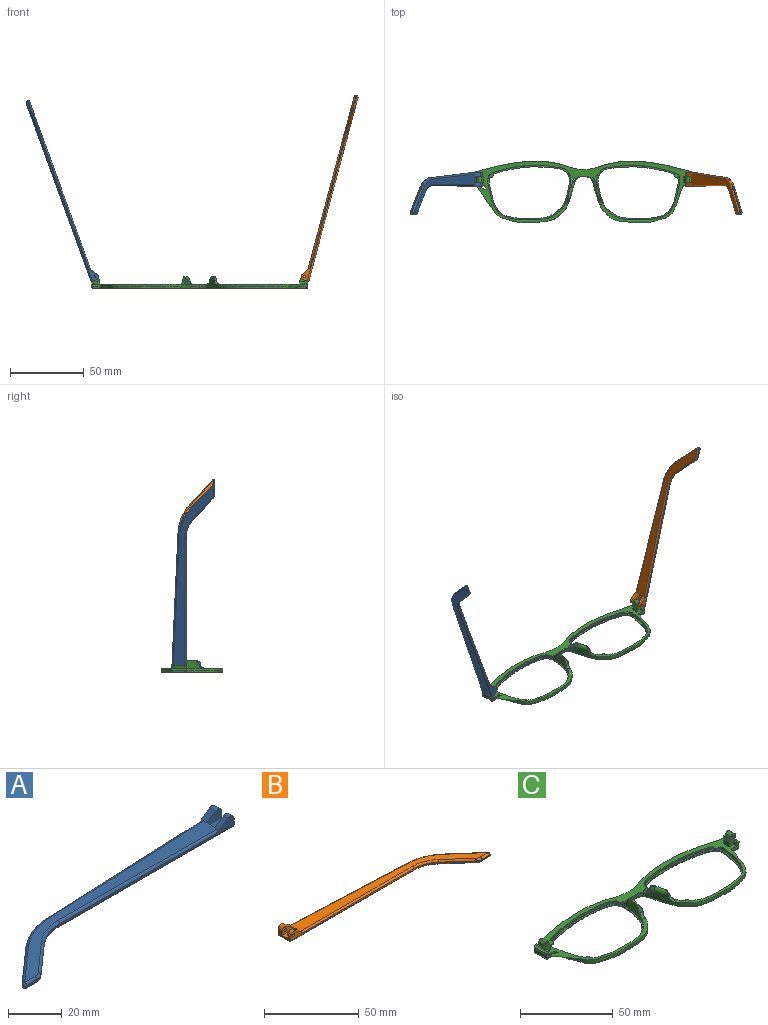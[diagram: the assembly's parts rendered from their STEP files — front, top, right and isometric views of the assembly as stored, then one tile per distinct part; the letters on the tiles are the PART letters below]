
ASSEMBLY  parts=3 mates=2
PART A: 43 faces, bbox 130.2x29.5x5.9 mm
  f0: plane 9.62x3.72mm, normal (1,0,0), area 24.7mm2, adj f1,f3,f4,f5,f10,f16,f18,f28
  f1: cylinder r=2.2mm len=3.45mm, axis (0,-1,0), area 11mm2, adj f0,f2,f4,f37
  f2: plane 6.01x3.91mm, normal (-0.55,0,0.84), area 12.7mm2, adj f1,f4,f9,f19,f37
  f3: plane 2.26x0.1mm, normal (0,0,1), area 0.1mm2, adj f0,f5,f18
  f4: plane 92.1x4.9mm, normal (0,-1,0), area 79.9mm2, adj f0,f1,f2,f14,f19,f36,f42
  f5: plane 93.42x4.13mm, normal (-0.04,1,0), area 64.8mm2, adj f0,f3,f11,f15,f17,f27,f28
  f6: plane 17.82x15.72mm, normal (-0.66,0.75,0), area 14.3mm2, adj f11,f12,f25,f30
  f7: plane 5.46x0.6mm, normal (0,-1,0), area 3.3mm2, adj f12,f13,f23,f32
  f8: plane 14.99x13.23mm, normal (0.66,-0.75,0), area 12mm2, adj f13,f14,f21,f34
  f9: plane 121.18x26.73mm, normal (0,0,1), area 627.7mm2, adj f2,f17,f19,f20,f21,f22,f23,f25
  f10: plane 129.1x27.08mm, normal (0,0,-1), area 686.5mm2, adj f0,f28,f29,f30,f32,f33,f34,f35
  f11: cylinder r=30mm len=18.52mm, axis (0,0,-1), area 12.2mm2, adj f5,f6,f26,f29
  f12: cylinder r=1mm len=1.75mm, axis (0,0,-1), area 1.5mm2, adj f6,f7,f24,f31
  f13: cylinder r=5mm len=3.31mm, axis (0,0,-1), area 2.2mm2, adj f7,f8,f22,f33
  f14: cylinder r=20mm len=13.23mm, axis (0,0,1), area 8.7mm2, adj f4,f8,f20,f35
  f15: plane 5.66x0.25mm, normal (0,0,-1), area 0.7mm2, adj f5,f17,f18
  f16: cylinder r=2.2mm len=3.45mm, axis (0,-1,0), area 14.8mm2, adj f0,f17,f18,f38
  f17: plane 6.01x3.91mm, normal (-0.55,0,0.84), area 16.9mm2, adj f5,f9,f15,f16,f18,f27,f38
  f18: plane 7.92x3.3mm, normal (0,1,0), area 15.9mm2, adj f0,f3,f15,f16,f17,f41
  f19: cylinder r=1mm len=84.18mm, axis (-1,0,0), area 131.4mm2, adj f2,f4,f9,f20
  f20: torus R=21mm, axis (0,0,1), area 23.1mm2, adj f9,f14,f19,f21
  f21: cylinder r=1mm len=15.65mm, axis (-0.75,-0.66,0), area 31.4mm2, adj f8,f9,f20,f22
  f22: torus R=4mm, axis (0,0,1), area 5.3mm2, adj f9,f13,f21,f23
  f23: cylinder r=1mm len=5.46mm, axis (-1,0,0), area 8.6mm2, adj f7,f9,f22,f24
  f24: sphere r=1mm, area 2.4mm2, adj f12,f23,f25
  f25: cylinder r=1mm len=18.48mm, axis (0.75,0.66,0), area 37.3mm2, adj f6,f9,f24,f26
  f26: torus R=29mm, axis (0,0,1), area 31.6mm2, adj f9,f11,f25,f27
  f27: cylinder r=1mm len=85.5mm, axis (1,0.04,0), area 133.5mm2, adj f5,f9,f17,f26
  f28: cylinder r=1mm len=93.46mm, axis (-1,-0.04,0), area 146.9mm2, adj f0,f5,f10,f29
  f29: torus R=29mm, axis (0,0,1), area 31.6mm2, adj f10,f11,f28,f30
  f30: cylinder r=1mm len=18.48mm, axis (-0.75,-0.66,0), area 37.3mm2, adj f6,f10,f29,f31
  f31: sphere r=1mm, area 2.4mm2, adj f12,f30,f32
  f32: cylinder r=1mm len=5.46mm, axis (1,0,0), area 8.6mm2, adj f7,f10,f31,f33
  f33: torus R=4mm, axis (0,0,1), area 5.3mm2, adj f10,f13,f32,f34
  f34: cylinder r=1mm len=15.65mm, axis (0.75,0.66,0), area 31.4mm2, adj f8,f10,f33,f35
  f35: torus R=21mm, axis (0,0,1), area 23.1mm2, adj f10,f14,f34,f36
  f36: cylinder r=1mm len=92.1mm, axis (1,0,0), area 144.7mm2, adj f0,f4,f10,f35
  f37: plane 7.92x4.7mm, normal (0,1,0), area 27mm2, adj f0,f1,f2,f39,f40,f42
  f38: plane 7.92x4.7mm, normal (0,-1,0), area 27mm2, adj f0,f16,f17,f39,f40,f41
  f39: plane 7.92x4.1mm, normal (0,0,1), area 32.5mm2, adj f0,f37,f38,f40
  f40: plane 4.1x1.4mm, normal (1,0,0), area 5.7mm2, adj f9,f37,f38,f39
  f41: cylinder r=0.5mm len=3.1mm, axis (0,-1,0), area 9.7mm2, adj f18,f38
  f42: cylinder r=0.5mm len=2.3mm, axis (0,-1,0), area 7.2mm2, adj f4,f37
PART B: 43 faces, bbox 130.2x29.5x5.9 mm
  f0: plane 9.62x3.72mm, normal (-1,0,0), area 24.7mm2, adj f1,f3,f4,f5,f10,f16,f18,f28
  f1: cylinder r=2.2mm len=3.45mm, axis (0,-1,0), area 11mm2, adj f0,f2,f4,f37
  f2: plane 6.01x3.91mm, normal (0.55,0,0.84), area 12.7mm2, adj f1,f4,f9,f19,f37
  f3: plane 2.26x0.1mm, normal (0,0,1), area 0.1mm2, adj f0,f5,f18
  f4: plane 92.1x4.9mm, normal (0,-1,0), area 78.2mm2, adj f0,f1,f2,f14,f19,f36,f42
  f5: plane 93.42x4.13mm, normal (0.04,1,0), area 64.8mm2, adj f0,f3,f11,f15,f17,f27,f28
  f6: plane 17.82x15.72mm, normal (0.66,0.75,0), area 14.3mm2, adj f11,f12,f25,f30
  f7: plane 5.46x0.6mm, normal (0,-1,0), area 3.3mm2, adj f12,f13,f23,f32
  f8: plane 14.99x13.23mm, normal (-0.66,-0.75,0), area 12mm2, adj f13,f14,f21,f34
  f9: plane 121.18x26.73mm, normal (0,0,1), area 627.7mm2, adj f2,f17,f19,f20,f21,f22,f23,f25
  f10: plane 129.1x27.08mm, normal (0,0,-1), area 686.5mm2, adj f0,f28,f29,f30,f32,f33,f34,f35
  f11: cylinder r=30mm len=18.52mm, axis (0,0,-1), area 12.2mm2, adj f5,f6,f26,f29
  f12: cylinder r=1mm len=1.75mm, axis (0,0,-1), area 1.5mm2, adj f6,f7,f24,f31
  f13: cylinder r=5mm len=3.31mm, axis (0,0,-1), area 2.2mm2, adj f7,f8,f22,f33
  f14: cylinder r=20mm len=13.23mm, axis (0,0,1), area 8.7mm2, adj f4,f8,f20,f35
  f15: plane 5.66x0.25mm, normal (0,0,-1), area 0.7mm2, adj f5,f17,f18
  f16: cylinder r=2.2mm len=3.45mm, axis (0,-1,0), area 14.8mm2, adj f0,f17,f18,f38
  f17: plane 6.01x3.91mm, normal (0.55,0,0.84), area 16.9mm2, adj f5,f9,f15,f16,f18,f27,f38
  f18: plane 7.92x3.3mm, normal (0,1,0), area 14.3mm2, adj f0,f3,f15,f16,f17,f41
  f19: cylinder r=1mm len=84.18mm, axis (1,0,0), area 131.4mm2, adj f2,f4,f9,f20
  f20: torus R=21mm, axis (0,0,1), area 23.1mm2, adj f9,f14,f19,f21
  f21: cylinder r=1mm len=15.65mm, axis (0.75,-0.66,0), area 31.4mm2, adj f8,f9,f20,f22
  f22: torus R=4mm, axis (0,0,1), area 5.3mm2, adj f9,f13,f21,f23
  f23: cylinder r=1mm len=5.46mm, axis (1,0,0), area 8.6mm2, adj f7,f9,f22,f24
  f24: sphere r=1mm, area 2.4mm2, adj f12,f23,f25
  f25: cylinder r=1mm len=18.48mm, axis (-0.75,0.66,0), area 37.3mm2, adj f6,f9,f24,f26
  f26: torus R=29mm, axis (0,0,1), area 31.6mm2, adj f9,f11,f25,f27
  f27: cylinder r=1mm len=85.5mm, axis (-1,0.04,0), area 133.5mm2, adj f5,f9,f17,f26
  f28: cylinder r=1mm len=93.46mm, axis (1,-0.04,0), area 146.9mm2, adj f0,f5,f10,f29
  f29: torus R=29mm, axis (0,0,1), area 31.6mm2, adj f10,f11,f28,f30
  f30: cylinder r=1mm len=18.48mm, axis (0.75,-0.66,0), area 37.3mm2, adj f6,f10,f29,f31
  f31: sphere r=1mm, area 2.4mm2, adj f12,f30,f32
  f32: cylinder r=1mm len=5.46mm, axis (-1,0,0), area 8.6mm2, adj f7,f10,f31,f33
  f33: torus R=4mm, axis (0,0,1), area 5.3mm2, adj f10,f13,f32,f34
  f34: cylinder r=1mm len=15.65mm, axis (-0.75,0.66,0), area 31.4mm2, adj f8,f10,f33,f35
  f35: torus R=21mm, axis (0,0,1), area 23.1mm2, adj f10,f14,f34,f36
  f36: cylinder r=1mm len=92.1mm, axis (-1,0,0), area 144.7mm2, adj f0,f4,f10,f35
  f37: plane 7.92x4.7mm, normal (0,1,0), area 25.4mm2, adj f0,f1,f2,f39,f40,f42
  f38: plane 7.92x4.7mm, normal (0,-1,0), area 25.4mm2, adj f0,f16,f17,f39,f40,f41
  f39: plane 7.92x4.1mm, normal (0,0,1), area 32.5mm2, adj f0,f37,f38,f40
  f40: plane 4.1x1.4mm, normal (-1,0,0), area 5.7mm2, adj f9,f37,f38,f39
  f41: cylinder r=0.88mm len=3.1mm, axis (0,-1,0), area 17mm2, adj f18,f38
  f42: cylinder r=0.88mm len=2.3mm, axis (0,-1,0), area 12.6mm2, adj f4,f37
PART C: 118 faces, bbox 148.1x42.9x17.9 mm
  f0: bspline ~2.65x2.04mm, area 1.9mm2, adj f1,f112,f113,f116,f117
  f1: bspline ~3.31x3.19mm, area 3.7mm2, adj f0,f2,f111,f112,f117
  f2: plane 147.69x42.46mm, normal (0,0,1), area 822.4mm2, adj f1,f3,f15,f16,f17,f18,f19,f20
  f3: plane 1.23x0.04mm, normal (0,0,1), area 0mm2, adj f2,f4,f113
  f4: plane 2.76x2.53mm, normal (0,-1,0), area 3.9mm2, adj f3,f5,f14,f15,f23
  f5: plane 9.65x1.24mm, normal (0,0,1), area 8.2mm2, adj f4,f6,f13,f14,f18,f19,f20,f23
  f6: plane 5.77x5.06mm, normal (0,-1,0), area 17mm2, adj f5,f7,f8,f10,f11,f12,f13,f22
  f7: cylinder r=1.98mm len=4mm, axis (0,-1,0), area 12.4mm2, adj f6,f11,f13,f20
  f8: plane 4x3.31mm, normal (-0.94,0,0.34), area 14.1mm2, adj f6,f9,f10,f20
  f9: plane 4x0.02mm, normal (0.34,0,0.94), area 0.1mm2, adj f8,f20,f21
  f10: cylinder r=1.98mm len=4mm, axis (0,1,0), area 12.4mm2, adj f6,f8,f11,f20
  f11: plane 4x0.01mm, normal (0.34,0,0.94), area 0mm2, adj f6,f7,f10,f20
  f12: cylinder r=0.88mm len=4mm, axis (0,-1,0), area 22mm2, adj f6,f20
  f13: plane 4x2.21mm, normal (0.94,0,-0.34), area 9.4mm2, adj f5,f6,f7,f20
  f14: plane 9.71x1.44mm, normal (0.34,0,0.94), area 13.9mm2, adj f4,f5,f15,f16,f17,f18
  f15: cone r=1mm half-angle=20deg, axis (0,0,1), area 2.3mm2, adj f2,f4,f14,f16
  f16: plane 7.67x1.6mm, normal (0.94,0,-0.34), area 13mm2, adj f2,f14,f15,f17
  f17: cylinder r=1mm len=2.28mm, axis (-0.34,0,-0.94), area 3mm2, adj f2,f14,f16,f18
  f18: plane 2.1x1.69mm, normal (0,1,0), area 2.8mm2, adj f2,f5,f14,f17,f19
  f19: plane 3.3x2.1mm, normal (-1,0,0), area 6.9mm2, adj f2,f5,f18,f20
  f20: plane 6.97x5.07mm, normal (0,1,0), area 22.7mm2, adj f2,f5,f7,f8,f9,f10,f11,f12
  f21: plane 4x2.36mm, normal (-1,0,0), area 9.5mm2, adj f2,f9,f20,f22
  f22: plane 3.2x2.36mm, normal (0,-1,0), area 5.7mm2, adj f2,f6,f21,f23
  f23: plane 2.35x2.1mm, normal (-1,0,0), area 4.9mm2, adj f2,f4,f5,f6,f22
  f24: bspline ~3.71x3.66mm, area 7.8mm2, adj f2,f25,f30,f38,f113
  f25: bspline ~7.26x7.26mm, area 6.6mm2, adj f24,f26,f30,f38
  f26: bspline ~11.17x5.09mm, area 21.4mm2, adj f25,f27,f30,f38,f113,f117
  f27: plane 3.58x0.96mm, normal (0,0,1), area 0.3mm2, adj f26,f28,f38
  f28: bspline ~15.5x15.35mm, area 6.4mm2, adj f27,f29,f38,f111,f117
  f29: extruded ~4.98x1.36mm, area 6.6mm2, adj f28,f38
  f30: extruded ~4.44x3.34mm, area 15.1mm2, adj f24,f25,f26,f31,f113
  f31: plane 4.46x1.44mm, normal (0,0,1), area 0.1mm2, adj f30,f113
  f32: cylinder r=1.3mm len=1.96mm, axis (0,0,1), area 1.7mm2, adj f2,f33,f38
  f33: plane 1.97x1.94mm, normal (0,0,-1), area 1.9mm2, adj f32,f38
  f34: cylinder r=1.3mm len=1.93mm, axis (0,0,1), area 1.5mm2, adj f2,f35,f38
  f35: plane 1.95x1.68mm, normal (0,0,-1), area 1.5mm2, adj f34,f38
  f36: cylinder r=2.28mm len=3.54mm, axis (0,0,1), area 3.1mm2, adj f2,f37,f38
  f37: plane 3.57x3.57mm, normal (0,0,-1), area 7.9mm2, adj f36,f38
  f38: extruded ~56.3x36.96mm, area 217.4mm2, adj f2,f24,f25,f26,f27,f28,f29,f32
  f39: extruded ~56.3x36.96mm, area 162.1mm2, adj f38,f40
  f40: plane 56.6x37.05mm, normal (0,0,1), area 149.1mm2, adj f39,f41
  f41: bspline ~56.37x37.11mm, area 238.6mm2, adj f40,f42
  f42: plane 144.78x39.76mm, normal (0,0,-1), area 576.6mm2, adj f41,f43,f46,f49,f50,f51,f52,f54
  f43: bspline ~56.37x37.11mm, area 238.6mm2, adj f42,f44
  f44: plane 56.6x37.05mm, normal (0,0,1), area 149.1mm2, adj f43,f45
  f45: extruded ~56.3x36.96mm, area 162.1mm2, adj f44,f85
  f46: bspline ~8.63x1.2mm, area 12.6mm2, adj f42,f47,f48,f113
  f47: bspline ~1x1mm, area 0.8mm2, adj f46,f57,f113
  f48: bspline ~1.04x1mm, area 0.7mm2, adj f46,f49,f113
  f49: bspline ~45.87x8.59mm, area 59.8mm2, adj f42,f48,f50,f113
  f50: bspline ~37.2x6.7mm, area 56.6mm2, adj f42,f49,f51,f110
  f51: bspline ~37.2x6.7mm, area 56.6mm2, adj f42,f50,f52,f109
  f52: bspline ~45.87x8.59mm, area 59.8mm2, adj f42,f51,f53,f108
  f53: bspline ~1.04x1mm, area 0.8mm2, adj f52,f54,f108
  f54: bspline ~8.63x1.2mm, area 12.6mm2, adj f42,f53,f55,f108
  f55: bspline ~1x1mm, area 0.8mm2, adj f54,f56,f108
  f56: bspline ~73.17x32.29mm, area 163.8mm2, adj f42,f55,f57,f108
  f57: bspline ~73.17x32.29mm, area 163.8mm2, adj f42,f47,f56,f113
  f58: plane 3.19x1.37mm, normal (0,0,-1), area 2.1mm2, adj f38,f59
  f59: cylinder r=2.28mm len=3.17mm, axis (0,0,1), area 2.1mm2, adj f2,f38,f58,f111
  f60: bspline ~6.39x2.13mm, area 2.6mm2, adj f2,f61,f112,f113
  f61: bspline ~6.39x2.13mm, area 2.6mm2, adj f2,f60,f62,f108
  f62: bspline ~2.1x1.46mm, area 0.6mm2, adj f61,f63,f75,f108
  f63: bspline ~2.65x2.03mm, area 1.9mm2, adj f62,f64,f67,f75,f108
  f64: bspline ~2.11x1.35mm, area 0.7mm2, adj f63,f65,f67,f108
  f65: extruded ~3.67x3.11mm, area 5.9mm2, adj f64,f66,f67,f108
  f66: bspline ~5.24x1.75mm, area 0mm2, adj f65,f108
  f67: bspline ~6.22x5.12mm, area 12.6mm2, adj f63,f64,f65,f68,f73,f75,f108
  f68: bspline ~12.08x5.41mm, area 21.4mm2, adj f67,f69,f70,f72,f85,f108
  f69: plane 3.58x0.96mm, normal (0,0,1), area 0.3mm2, adj f68,f73,f85
  f70: extruded ~4.44x3.34mm, area 15.1mm2, adj f68,f71,f72,f86,f108
  f71: plane 4.46x1.44mm, normal (0,0,1), area 0.1mm2, adj f70,f108
  f72: bspline ~7.26x7.26mm, area 6.5mm2, adj f68,f70,f85,f86
  f73: bspline ~15.5x15.35mm, area 6.4mm2, adj f67,f69,f74,f76,f85
  f74: extruded ~4.98x1.36mm, area 6.6mm2, adj f73,f85
  f75: bspline ~3.55x3.47mm, area 3.7mm2, adj f2,f62,f63,f67,f76
  f76: bspline ~5.94x4.42mm, area 7.9mm2, adj f2,f73,f75,f77,f85
  f77: cylinder r=2.28mm len=3.17mm, axis (0,0,1), area 2.1mm2, adj f2,f76,f78,f85
  f78: plane 3.19x1.37mm, normal (0,0,-1), area 2.1mm2, adj f77,f85
  f79: cylinder r=2.28mm len=3.54mm, axis (0,0,1), area 3.1mm2, adj f2,f80,f85
  f80: plane 3.57x3.57mm, normal (0,0,-1), area 7.9mm2, adj f79,f85
  f81: cylinder r=1.3mm len=1.93mm, axis (0,0,1), area 1.5mm2, adj f2,f82,f85
  f82: plane 1.95x1.68mm, normal (0,0,-1), area 1.5mm2, adj f81,f85
  f83: cylinder r=1.3mm len=1.96mm, axis (0,0,1), area 1.7mm2, adj f2,f84,f85
  f84: plane 1.97x1.94mm, normal (0,0,-1), area 1.9mm2, adj f83,f85
  f85: extruded ~56.3x36.96mm, area 217.5mm2, adj f2,f45,f68,f69,f72,f73,f74,f76
  f86: bspline ~3.71x3.66mm, area 7.8mm2, adj f2,f70,f72,f85,f108
  f87: plane 2.35x2.1mm, normal (1,0,0), area 4.9mm2, adj f2,f88,f90,f97,f99
  f88: plane 2.76x2.53mm, normal (0,-1,0), area 3.9mm2, adj f87,f89,f90,f106,f107
  f89: plane 9.71x1.44mm, normal (-0.34,0,0.94), area 13.9mm2, adj f88,f90,f103,f104,f105,f106
  f90: plane 9.65x1.24mm, normal (0,0,1), area 8.2mm2, adj f87,f88,f89,f91,f97,f101,f102,f103
  f91: plane 4x2.21mm, normal (-0.94,0,-0.34), area 9.4mm2, adj f90,f92,f97,f101
  f92: cylinder r=1.98mm len=4mm, axis (0,-1,0), area 12.4mm2, adj f91,f93,f97,f101
  f93: plane 4x0.01mm, normal (-0.34,0,0.94), area 0mm2, adj f92,f94,f97,f101
  f94: cylinder r=1.98mm len=4mm, axis (0,1,0), area 12.4mm2, adj f93,f95,f97,f101
  f95: plane 4x3.31mm, normal (0.94,0,0.34), area 14.1mm2, adj f94,f96,f97,f101
  f96: plane 4x0.02mm, normal (-0.34,0,0.94), area 0.1mm2, adj f95,f100,f101
  f97: plane 5.77x5.06mm, normal (0,-1,0), area 17mm2, adj f87,f90,f91,f92,f93,f94,f95,f98
  f98: cylinder r=0.88mm len=4mm, axis (0,-1,0), area 22mm2, adj f97,f101
  f99: plane 3.2x2.36mm, normal (0,-1,0), area 5.7mm2, adj f2,f87,f97,f100
  f100: plane 4x2.36mm, normal (1,0,0), area 9.5mm2, adj f2,f96,f99,f101
  f101: plane 6.97x5.07mm, normal (0,1,0), area 22.7mm2, adj f2,f90,f91,f92,f93,f94,f95,f96
  f102: plane 3.3x2.1mm, normal (1,0,0), area 6.9mm2, adj f2,f90,f101,f103
  f103: plane 2.1x1.69mm, normal (0,1,0), area 2.8mm2, adj f2,f89,f90,f102,f104
  f104: cylinder r=1mm len=2.28mm, axis (0.34,0,-0.94), area 3mm2, adj f2,f89,f103,f105
  f105: plane 7.67x1.6mm, normal (-0.94,0,-0.34), area 13mm2, adj f2,f89,f104,f106
  f106: cone r=1mm half-angle=20deg, axis (0,0,1), area 2.3mm2, adj f2,f88,f89,f105
  f107: plane 1.23x0.04mm, normal (0,0,1), area 0mm2, adj f2,f88,f108
  f108: extruded ~73.28x41.69mm, area 294mm2, adj f2,f52,f53,f54,f55,f56,f61,f62
  f109: extruded ~35.39x5.69mm, area 72.2mm2, adj f2,f51,f108,f110
  f110: extruded ~35.39x5.69mm, area 72.2mm2, adj f2,f50,f109,f113
  f111: bspline ~6.16x4.45mm, area 7.9mm2, adj f1,f2,f28,f38,f59
  f112: bspline ~2.1x1.46mm, area 0.6mm2, adj f0,f1,f60,f113
  f113: extruded ~73.28x41.69mm, area 294mm2, adj f0,f2,f3,f24,f26,f30,f31,f46
  f114: bspline ~5.24x1.75mm, area 0mm2, adj f113,f115
  f115: extruded ~3.67x3.11mm, area 5.9mm2, adj f113,f114,f116,f117
  f116: bspline ~1.73x1.17mm, area 0.7mm2, adj f0,f113,f115,f117
  f117: bspline ~6.22x5.12mm, area 12.6mm2, adj f0,f1,f26,f28,f113,f115,f116
PLACE A rot(axis=(0,1,0),70deg) t=(-84.77,-5.75,56)mm
PLACE B rot(axis=(0,-1,0),75deg) t=(68.2,-5.75,-61.61)mm
PLACE C t=(10.15,-1.13,-5.77)mm
MATE revolute A.f1 <-> C.f94  axis (0,-1,0) through (-60.89,2.72,1.22)mm
MATE revolute B.f41 <-> C.f7  axis (0,-1,0) through (81.2,2.72,1.21)mm
